# Revit family: Furniture-Mirror_Shelf-KOHLER-URBANITY-K-99916T
name_source: partatom
category: Specialty Equipment
units: mm (PartAtom-declared; Revit-internal decimal feet)

## family parameters
Cut with Voids When Loaded = No
Host = Face
OmniClass Number = 23.31.25.00
OmniClass Title = Toilet and Bath Specialties
Part Type = Normal
Room Calculation Point = No
Round Connector Dimension = Use Diameter
Shared = No

## types (2) — shared parameters
ADA Compliant = No
Assembly Code = C1030200
Date Modified = 01/28/2023
Default Elevation = 60"
Description = STARS ARE OPEN CABINETS
Height = 8 3/8"
Length = 3 3/4"
Manufacturer = Kohler Co.
Master Format 2014 = 10 28 00
Master Format 2014 Name = Toilet, Bath, and Laundry Accessories
Material = Aluminium
Product Name = URBANITY
URL = http://www.kohler.com.cn
WaterSense Certified = No
Width = 35 7/16"

## per-type parameters (varying)
| type | Finish | Model | Product Documentation Link | Product Page URL | Type |
| NA-Black | Kohler-Metal-NA-Black | K-99916T-NA |  |  | 1 |
| LK-Black | KOHLER-Metal-LK-Black | K-99916T-LK | https://files.kohler.com.cn | https://www.kohler.com.cn | 2 |

## geometry (parser evidence)
native form markers: Sweep x6
no freeform markers — native parametric forms only
